# Revit family: Result Chair
name_source: partatom
category: Furniture
revit_build: Autodesk Revit 2016 (Build: 20161004_0715(x64)
units: mm (PartAtom-declared; Revit-internal decimal feet)

## family parameters
Always vertical = Yes
Cut with Voids When Loaded = No
OmniClass Number = 23.40.20.00
OmniClass Title = General Furniture and Specialties
Room Calculation Point = No
Shared = No
Work Plane-Based = No

## types (1)
- Result Chair
    Backrest = HAY Clear lacquered oak veneer Vertical
    Base = HAY Black powder coated aluminum - Soft Black
    Depth = 48.5cm - 19.0inch
    Description = Modern relaunch of Friso Kramer and Wim Rietveld’s 1950s design for Ahrend featuring a thin sheet steel base and oak veneer seat and back. Suitable for schools, institutions and public spaces, as well as in private settings.
    Design = Friso Kramer & Wim Rietveld
    Fittings = HAY Black Plastic
    Gliders = HAY Black Plastic
    Height = 81cm - 19.0inch
    Manufacturer = HAY
    Model = Result Chair
    Optional gliders = Felt glider
    Price = Contact HAY or visit hay.dk
    Screws = HAY Chrome
    Seat = HAY Clear lacquered oak veneer
    Seat Height = 46cm - 18.11inch
    Strength, durability and safety = EN 16139:2013 L2
    Type Comments = Moulded plywood seat and back. Top veneer in oak. Steel sheet legs
    URL = https://hay.dk
    Variations = Available in a variety of wood finishes and base colours that can be combined with the Pyramid Table or other tables in the HAY collection.
    Width = 45.5cm - 17.9inch

## geometry (parser evidence)
native form markers: Sweep x3
no freeform markers — native parametric forms only
